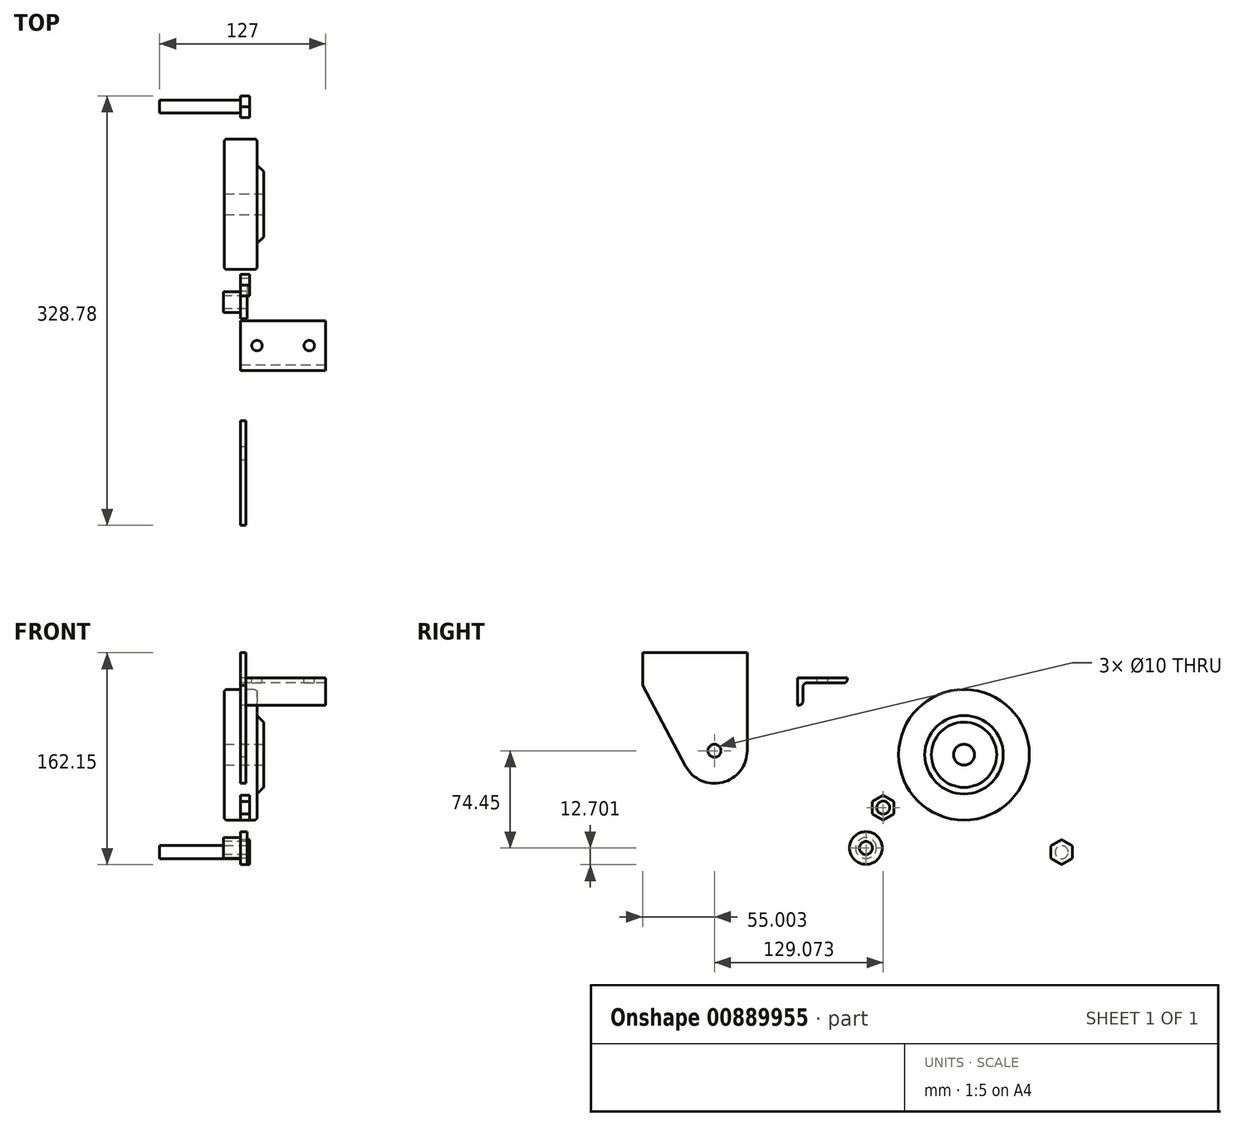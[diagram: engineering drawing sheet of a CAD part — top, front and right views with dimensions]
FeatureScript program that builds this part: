
annotation { "Feature Type Name" : "Feature", "Feature Type Description" : "" }
export const myFeature = defineFeature(function(context is Context, id is Id, definition is map)
    precondition{}
    {
        {
            var Q0;
            Q0=qCreatedBy(makeId("Right.planeOp"),FACE);
            var sketch = newSketch(context, id + "F0", { "sketchPlane" : qUnion([Q0])});
            skCircle(sketch, "E0", {"center": v(0, 0) * mm, "radius": 50 * mm});
            skSolve(sketch);
        }
        {
            var Q0;
            Q0=makeQuery(id+"F0.imprint","IMPRINT",FACE,{"disambiguationData":[TD([[makeQuery(id+"F0.imprint","IMPRINT",EDGE,{"derivedFrom":sQuery(id+"F0.wireOp",EDGE,"E0")}),1.0]])]});
            extrude(context, id + "F1", {"entities" : qUnion([Q0]), "endBound" : BoundingType.SYMMETRIC, "depth" : 25 * mm, "offsetDistance" : 25 * mm});
        }
        {
            var Q0;
            Q0=makeQuery(id+"F1.opExtrude","CAP_FACE",FACE,{"disambiguationData":[OSD([sQuery(id+"F0.wireOp",EDGE,"E0")])],"isStart":false});
            var sketch = newSketch(context, id + "F2", { "sketchPlane" : qUnion([Q0])});
            skCircle(sketch, "E1", {"center": v(0, 0) * mm, "radius": 30 * mm});
            skSolve(sketch);
        }
        {
            var Q0;
            Q0=makeQuery(id+"F2.imprint","IMPRINT",FACE,{"disambiguationData":[TD([[makeQuery(id+"F2.imprint","IMPRINT",EDGE,{"derivedFrom":sQuery(id+"F2.wireOp",EDGE,"E1")}),1.0]])]});
            extrude(context, id + "F3", {"entities" : qUnion([Q0]), "operationType" : NewBodyOperationType.ADD, "depth" : 5 * mm, "offsetDistance" : 25 * mm, "hasDraft" : true, "draftAngle" : 45 * degree, "draftPullDirection" : true});
        }
        {
            var Q0;
            Q0=makeQuery(id+"F1.opExtrude","CAP_EDGE",EDGE,{"disambiguationData":[OSD([sQuery(id+"F0.wireOp",EDGE,"E0")])],"isStart":false});
            var Q1;
            Q1=makeQuery(id+"F1.opExtrude","CAP_EDGE",EDGE,{"disambiguationData":[OSD([sQuery(id+"F0.wireOp",EDGE,"E0")])],"isStart":true});
            fillet(context, id + "F4", {"entities" : qUnion([Q0, Q1]), "radius" : 2 * mm, "tangentPropagation" : true, "allowEdgeOverflow" : false});
        }
        {
            var Q0;
            Q0=qCreatedBy(makeId("Right.planeOp"),FACE);
            var sketch = newSketch(context, id + "F5", { "sketchPlane" : qUnion([Q0])});
            skCircle(sketch, "E2", {"center": v(0, 0) * mm, "radius": 8 * mm});
            skSolve(sketch);
        }
        {
            var Q0;
            Q0 = qSketchRegion(id + "F5", true);
            extrude(context, id + "F6", {"entities" : qUnion([Q0]), "operationType" : NewBodyOperationType.REMOVE, "endBound" : BoundingType.THROUGH_ALL, "oppositeDirection" : true, "depth" : 25 * mm, "offsetDistance" : 25 * mm, "hasSecondDirection" : true, "secondDirectionBound" : SecondDirectionBoundingType.THROUGH_ALL, "secondDirectionOppositeDirection" : false, "secondDirectionDepth" : 25 * mm});
        }
        {
            var Q0;
            Q0=qCreatedBy(makeId("Right.planeOp"),FACE);
            var sketch = newSketch(context, id + "F7", { "sketchPlane" : qUnion([Q0])});
            skCircle(sketch, "E3", {"center": v(-75.02, -71.39) * mm, "radius": 12.5 * mm});
            skCircle(sketch, "E4", {"center": v(-75.02, -71.39) * mm, "radius": 8 * mm});
            skCircle(sketch, "E5", {"center": v(-75.02, -71.39) * mm, "radius": 5 * mm});
            skSolve(sketch);
        }
        {
            var Q0;
            Q0=makeQuery(id+"F7.imprint","IMPRINT",FACE,{"disambiguationData":[TD([[makeQuery(id+"F7.imprint","IMPRINT",EDGE,{"derivedFrom":sQuery(id+"F7.wireOp",EDGE,"E3")}),1.0]])]});
            var Q1;
            Q1=makeQuery(id+"F7.imprint","IMPRINT",FACE,{"disambiguationData":[TD([[makeQuery(id+"F7.imprint","IMPRINT",EDGE,{"derivedFrom":sQuery(id+"F7.wireOp",EDGE,"E4")}),1.0]])]});
            extrude(context, id + "F8", {"entities" : qUnion([Q0, Q1]), "depth" : 5 * mm, "offsetDistance" : 25 * mm});
        }
        {
            var Q0;
            Q0=makeQuery(id+"F7.imprint","IMPRINT",FACE,{"disambiguationData":[TD([[makeQuery(id+"F7.imprint","IMPRINT",EDGE,{"derivedFrom":sQuery(id+"F7.wireOp",EDGE,"E4")}),1.0]])]});
            extrude(context, id + "F9", {"entities" : qUnion([Q0]), "operationType" : NewBodyOperationType.ADD, "oppositeDirection" : true, "depth" : (18 - 5) * mm, "offsetDistance" : 25 * mm});
        }
        {
            var Q0;
            Q0=qCreatedBy(makeId("Right.planeOp"),FACE);
            var sketch = newSketch(context, id + "F10", { "sketchPlane" : qUnion([Q0])});
            skCircle(sketch, "E6", {"center": v(74.7, -74.59) * mm, "radius": 5 * mm});
            skCircle(sketch, "E7.cCircle", {"center": v(74.7, -74.59) * mm, "radius": 9.5 * mm, "construction": true});
            skLineSegment(sketch, "E7.0", {"start": v(74.7, -65.08) * mm, "end": v(82.92, -69.83) * mm});
            skLineSegment(sketch, "E7.1", {"start": v(82.92, -69.83) * mm, "end": v(82.92, -79.34) * mm});
            skLineSegment(sketch, "E7.2", {"start": v(82.92, -79.34) * mm, "end": v(74.7, -84.1) * mm});
            skLineSegment(sketch, "E7.3", {"start": v(74.7, -84.1) * mm, "end": v(66.46, -79.34) * mm});
            skLineSegment(sketch, "E7.4", {"start": v(66.46, -79.34) * mm, "end": v(66.46, -69.83) * mm});
            skLineSegment(sketch, "E7.5", {"start": v(66.46, -69.83) * mm, "end": v(74.7, -65.08) * mm});
            skSolve(sketch);
        }
        {
            var Q0;
            Q0=makeQuery(id+"F10.imprint","IMPRINT",FACE,{"disambiguationData":[TD([[makeQuery(id+"F10.imprint","IMPRINT",EDGE,{"derivedFrom":sQuery(id+"F10.wireOp",EDGE,"E6")}),-1.0]])]});
            var Q1;
            Q1=makeQuery(id+"F10.imprint","IMPRINT",FACE,{"disambiguationData":[TD([[makeQuery(id+"F10.imprint","IMPRINT",EDGE,{"derivedFrom":sQuery(id+"F10.wireOp",EDGE,"E6")}),1.0]])]});
            extrude(context, id + "F11", {"entities" : qUnion([Q0, Q1]), "depth" : 7 * mm, "offsetDistance" : 25 * mm});
        }
        {
            var Q0;
            Q0=makeQuery(id+"F10.imprint","IMPRINT",FACE,{"disambiguationData":[TD([[makeQuery(id+"F10.imprint","IMPRINT",EDGE,{"derivedFrom":sQuery(id+"F10.wireOp",EDGE,"E6")}),1.0]])]});
            extrude(context, id + "F12", {"entities" : qUnion([Q0]), "operationType" : NewBodyOperationType.ADD, "oppositeDirection" : true, "depth" : 62 * mm, "offsetDistance" : 25 * mm});
        }
        {
            var Q0;
            Q0=qCreatedBy(makeId("Right.planeOp"),FACE);
            var sketch = newSketch(context, id + "F13", { "sketchPlane" : qUnion([Q0])});
            skCircle(sketch, "E8", {"center": v(-61.78, -40.48) * mm, "radius": 5 * mm});
            skCircle(sketch, "E9.cCircle", {"center": v(-61.78, -40.48) * mm, "radius": 9.5 * mm, "construction": true});
            skLineSegment(sketch, "E9.0", {"start": v(-61.78, -30.98) * mm, "end": v(-53.55, -35.73) * mm});
            skLineSegment(sketch, "E9.1", {"start": v(-53.55, -35.73) * mm, "end": v(-53.55, -45.24) * mm});
            skLineSegment(sketch, "E9.2", {"start": v(-53.55, -45.24) * mm, "end": v(-61.78, -49.99) * mm});
            skLineSegment(sketch, "E9.3", {"start": v(-61.78, -49.99) * mm, "end": v(-70.02, -45.24) * mm});
            skLineSegment(sketch, "E9.4", {"start": v(-70.02, -45.24) * mm, "end": v(-70.02, -35.73) * mm});
            skLineSegment(sketch, "E9.5", {"start": v(-70.02, -35.73) * mm, "end": v(-61.78, -30.98) * mm});
            skSolve(sketch);
        }
        {
            var Q0;
            Q0=makeQuery(id+"F13.imprint","IMPRINT",FACE,{"disambiguationData":[TD([[makeQuery(id+"F13.imprint","IMPRINT",EDGE,{"derivedFrom":sQuery(id+"F13.wireOp",EDGE,"E8")}),-1.0]])]});
            extrude(context, id + "F14", {"entities" : qUnion([Q0]), "depth" : 7 * mm, "offsetDistance" : 25 * mm});
        }
        {
            var Q0;
            Q0=qCreatedBy(makeId("Right.planeOp"),FACE);
            var sketch = newSketch(context, id + "F15", { "sketchPlane" : qUnion([Q0])});
            skArc(sketch, "E10", {"start": v(-212.92, -8.7) * mm, "mid": v(-184.8, -21.2) * mm, "end": v(-165.86, 3.06) * mm});
            skLineSegment(sketch, "E11", {"start": v(-165.86, 3.06) * mm, "end": v(-165.86, 78.06) * mm});
            skLineSegment(sketch, "E12", {"start": v(-245.86, 78.06) * mm, "end": v(-165.86, 78.06) * mm});
            skLineSegment(sketch, "E13", {"start": v(-245.86, 78.06) * mm, "end": v(-245.86, 53.06) * mm});
            skLineSegment(sketch, "E14", {"start": v(-245.86, 53.06) * mm, "end": v(-212.92, -8.7) * mm});
            skCircle(sketch, "E15", {"center": v(-190.86, 3.06) * mm, "radius": 5 * mm});
            skSolve(sketch);
        }
        {
            var Q0;
            Q0=makeQuery(id+"F15.imprint","IMPRINT",FACE,{"disambiguationData":[TD([[makeQuery(id+"F15.imprint","IMPRINT",EDGE,{"derivedFrom":sQuery(id+"F15.wireOp",EDGE,"E10")}),1.0]])]});
            extrude(context, id + "F16", {"entities" : qUnion([Q0]), "depth" : 4 * mm, "offsetDistance" : 25 * mm});
        }
        {
            var Q0;
            Q0=qCreatedBy(makeId("Right.planeOp"),FACE);
            var sketch = newSketch(context, id + "F17", { "sketchPlane" : qUnion([Q0])});
            skLineSegment(sketch, "E16", {"start": v(-89.24, 58.92) * mm, "end": v(-127.24, 58.92) * mm});
            skLineSegment(sketch, "E17", {"start": v(-127.24, 37.92) * mm, "end": v(-127.24, 58.92) * mm});
            skLineSegment(sketch, "E18.0", {"start": v(-123.24, 40.92) * mm, "end": v(-123.24, 51.92) * mm});
            skLineSegment(sketch, "E18.1", {"start": v(-92.24, 54.92) * mm, "end": v(-120.24, 54.92) * mm});
            skLineSegment(sketch, "E19", {"start": v(-89.24, 58.92) * mm, "end": v(-89.24, 57.92) * mm});
            skLineSegment(sketch, "E20", {"start": v(-126.24, 37.92) * mm, "end": v(-127.24, 37.92) * mm});
            skPoint(sketch, "E21.visualSharp", {"position": v(-123.24, 54.92) * mm});
            skArc(sketch, "E21.filletArc", {"start": v(-120.24, 54.92) * mm, "mid": v(-122.36, 54.05) * mm, "end": v(-123.24, 51.92) * mm});
            skPoint(sketch, "E22.visualSharp", {"position": v(-123.24, 37.92) * mm});
            skArc(sketch, "E22.filletArc", {"start": v(-126.24, 37.92) * mm, "mid": v(-124.12, 38.8) * mm, "end": v(-123.24, 40.92) * mm});
            skPoint(sketch, "E23.visualSharp", {"position": v(-89.24, 54.92) * mm});
            skArc(sketch, "E23.filletArc", {"start": v(-92.24, 54.92) * mm, "mid": v(-90.12, 55.8) * mm, "end": v(-89.24, 57.92) * mm});
            skSolve(sketch);
        }
        {
            var Q0;
            Q0=makeQuery(id+"F17.imprint","IMPRINT",FACE,{"disambiguationData":[TD([[makeQuery(id+"F17.imprint","IMPRINT",EDGE,{"derivedFrom":sQuery(id+"F17.wireOp",EDGE,"E16")}),1.0]])]});
            extrude(context, id + "F18", {"entities" : qUnion([Q0]), "depth" : 65 * mm, "offsetDistance" : 25 * mm});
        }
        {
            var Q0;
            Q0=makeQuery(id+"F18.opExtrude","SWEPT_FACE",FACE,{"disambiguationData":[OSD([sQuery(id+"F17.wireOp",EDGE,"E16")])]});
            var sketch = newSketch(context, id + "F19", { "sketchPlane" : qUnion([Q0])});
            skLineSegment(sketch, "E24", {"start": v(65, -108.24) * mm, "end": v(0, -108.24) * mm, "construction": true});
            skLineSegment(sketch, "E25", {"start": v(32.5, -89.24) * mm, "end": v(32.5, -127.24) * mm, "construction": true});
            skLineSegment(sketch, "E26.0", {"start": v(52.5, -89.24) * mm, "end": v(52.5, -127.24) * mm, "construction": true});
            skLineSegment(sketch, "E27.MirrorCS", {"start": v(12.5, -89.24) * mm, "end": v(12.5, -127.24) * mm, "construction": true});
            skCircle(sketch, "E28", {"center": v(52.5, -108.24) * mm, "radius": 4 * mm});
            skCircle(sketch, "E29", {"center": v(12.5, -108.24) * mm, "radius": 4 * mm});
            skSolve(sketch);
        }
        {
            var Q0;
            Q0=makeQuery(id+"F19.imprint","IMPRINT",FACE,{"disambiguationData":[TD([[makeQuery(id+"F19.imprint","IMPRINT",EDGE,{"derivedFrom":sQuery(id+"F19.wireOp",EDGE,"E28")}),1.0]])]});
            var Q1;
            Q1=makeQuery(id+"F19.imprint","IMPRINT",FACE,{"disambiguationData":[TD([[makeQuery(id+"F19.imprint","IMPRINT",EDGE,{"derivedFrom":sQuery(id+"F19.wireOp",EDGE,"E29")}),1.0]])]});
            extrude(context, id + "F20", {"entities" : qUnion([Q0, Q1]), "operationType" : NewBodyOperationType.REMOVE, "oppositeDirection" : true, "depth" : 25 * mm, "offsetDistance" : 25 * mm});
        }
    });
